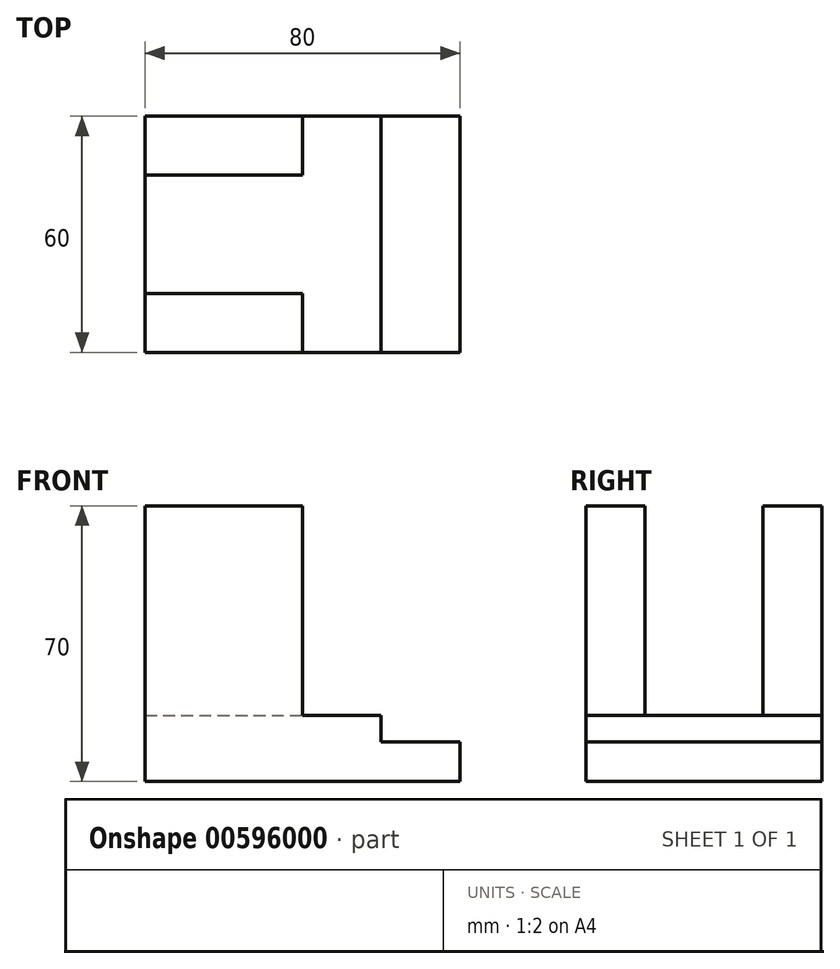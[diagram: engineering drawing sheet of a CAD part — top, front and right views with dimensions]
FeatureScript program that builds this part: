
annotation { "Feature Type Name" : "Feature", "Feature Type Description" : "" }
export const myFeature = defineFeature(function(context is Context, id is Id, definition is map)
    precondition{}
    {
        {
            var Q0;
            Q0=qCreatedBy(makeId("Front.planeOp"),FACE);
            var sketch = newSketch(context, id + "F0", { "sketchPlane" : qUnion([Q0])});
            skLineSegment(sketch, "E0", {"start": v(-38.75, 23.7) * mm, "end": v(-38.75, -46.3) * mm});
            skLineSegment(sketch, "E1", {"start": v(-38.75, -46.3) * mm, "end": v(41.25, -46.3) * mm});
            skLineSegment(sketch, "E2", {"start": v(41.25, -46.3) * mm, "end": v(41.25, -36.3) * mm});
            skLineSegment(sketch, "E3", {"start": v(41.25, -36.3) * mm, "end": v(21.25, -36.3) * mm});
            skLineSegment(sketch, "E4", {"start": v(21.25, -36.3) * mm, "end": v(21.25, -29.56) * mm});
            skLineSegment(sketch, "E5", {"start": v(21.25, -29.56) * mm, "end": v(1.25, -29.56) * mm});
            skLineSegment(sketch, "E6", {"start": v(1.25, -29.56) * mm, "end": v(1.25, 23.7) * mm});
            skLineSegment(sketch, "E7", {"start": v(1.25, 23.7) * mm, "end": v(-38.75, 23.7) * mm});
            skSolve(sketch);
        }
        {
            var Q0;
            Q0 = qSketchRegion(id + "F0", true);
            extrude(context, id + "F1", {"entities" : qUnion([Q0]), "depth" : 60 * mm, "offsetDistance" : 25 * mm});
        }
        {
            var Q0;
            Q0=makeQuery(id+"F1.opExtrude","SWEPT_FACE",FACE,{"disambiguationData":[OSD([sQuery(id+"F0.wireOp",EDGE,"E6")])]});
            var sketch = newSketch(context, id + "F2", { "sketchPlane" : qUnion([Q0])});
            skLineSegment(sketch, "E8", {"start": v(-45, 23.7) * mm, "end": v(-45, -29.56) * mm});
            skLineSegment(sketch, "E9", {"start": v(-15, 23.7) * mm, "end": v(-15, -29.56) * mm});
            skSolve(sketch);
        }
        {
            var Q0;
            {var subQ0=sQuery(id+"F2.wireOp",EDGE,"E8");Q0=makeQuery(id+"F2.imprint","IMPRINT",FACE,{"disambiguationData":[TD([[makeQuery(id+"F2.imprint","IMPRINT",EDGE,{"derivedFrom":subQ0}),1.0]])]});}
            extrude(context, id + "F3", {"entities" : qUnion([Q0]), "operationType" : NewBodyOperationType.REMOVE, "endBound" : BoundingType.THROUGH_ALL, "oppositeDirection" : true, "depth" : 25 * mm, "offsetDistance" : 25 * mm});
        }
    });
